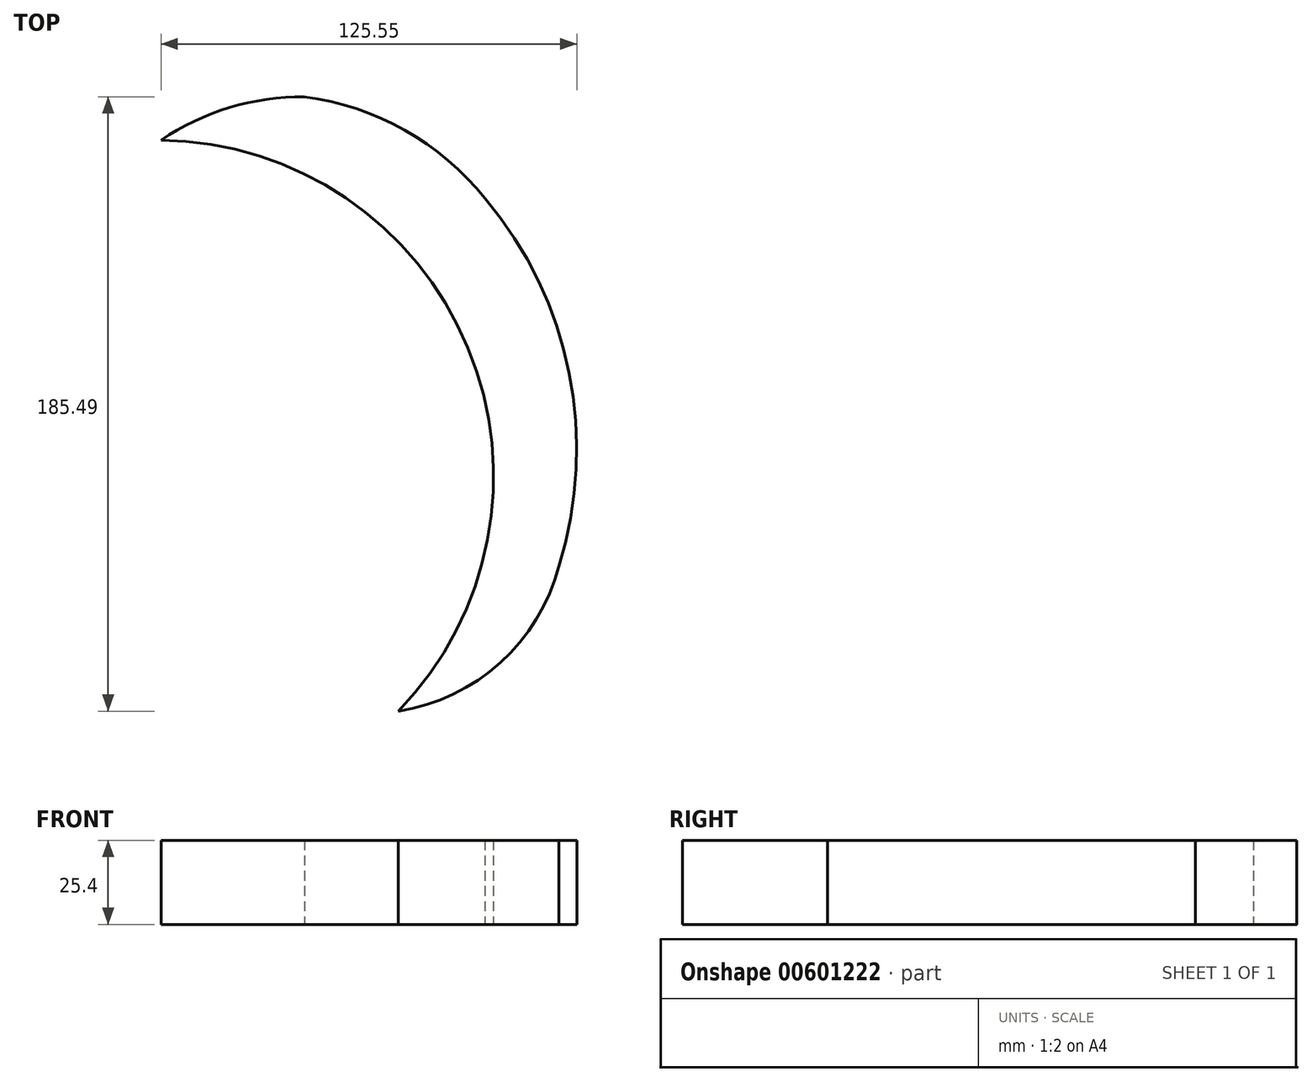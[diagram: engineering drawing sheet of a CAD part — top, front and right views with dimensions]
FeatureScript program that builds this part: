
annotation { "Feature Type Name" : "Feature", "Feature Type Description" : "" }
export const myFeature = defineFeature(function(context is Context, id is Id, definition is map)
    precondition{}
    {
        {
            var Q0;
            Q0=qCreatedBy(makeId("Top.planeOp"),FACE);
            var sketch = newSketch(context, id + "F0", { "sketchPlane" : qUnion([Q0])});
            skArc(sketch, "E0", {"start": v(-33.42, -57.62) * mm, "mid": v(-12.43, 52.2) * mm, "end": v(-105.06, 114.8) * mm});
            skArc(sketch, "E1", {"start": v(-61.72, 127.86) * mm, "mid": v(-84.38, 124.63) * mm, "end": v(-105.06, 114.8) * mm});
            skArc(sketch, "E2", {"start": v(-7.21, 97.23) * mm, "mid": v(-31.5, 117.83) * mm, "end": v(-61.72, 127.86) * mm});
            skArc(sketch, "E3", {"start": v(15.07, -13.81) * mm, "mid": v(18.2, 44.57) * mm, "end": v(-7.21, 97.23) * mm});
            skArc(sketch, "E4", {"start": v(-33.42, -57.62) * mm, "mid": v(-2.61, -42.98) * mm, "end": v(15.07, -13.81) * mm});
            skSolve(sketch);
        }
        {
            var Q0;
            Q0=makeQuery(id+"F0.imprint","IMPRINT",FACE,{"disambiguationData":[TD([[makeQuery(id+"F0.imprint","IMPRINT",EDGE,{"derivedFrom":sQuery(id+"F0.wireOp",EDGE,"E0")}),-1.0]])]});
            extrude(context, id + "F1", {"entities" : qUnion([Q0]), "depth" : 25.4 * mm, "offsetDistance" : 25.4 * mm});
        }
    });
